# Revit family: CLEVERTRONICS L10 OPTIMUM LIFELIGHT PRO_non_hosted_R16
name_source: partatom
category: Lighting Fixtures
revit_build: Autodesk Revit LT 2016 (Build: 20150220_1215(x64)
units: mm (PartAtom-declared; Revit-internal decimal feet)

## family parameters
Always vertical = Yes
Cut with Voids When Loaded = No
Light Source = Yes
OmniClass Number = 23.80.70.00
OmniClass Title = Lighting
Part Type = Normal
Room Calculation Point = No
Round Connector Dimension = Use Diameter
Shared = No
Work Plane-Based = No

## types (1)
- LLIFE-PRO-SMC
    AS/NZ2293 Classification = C0=D63 C90=D63
    Catalogue Number = LLIFE-PRO-SMC
    Charging Method = Intelligent current limited constant voltage charger
    Color Filter = 16777215
    Description = Lifelight PRO, High Performance, Cylinder Surface Mount Emergency Light with Lithium Battery Technology
    Dimensions L x W x H = 128mm (D), 252mm (L)
    Dimming Lamp Color Temperature Shift = <None>
    IP Rating = IP20
    Lamp = 2 x 3W LED (Lifetime warranty on the lamp head and loom assembly)
2 x 3W LED (Lifetime warranty on the lamp head and loom assembly)
No dome cover required
    Mounting = Surface Mount
    Operating Mode = Non-Maintained
    Operating Temperature = 1 to 40C (Ambient)
    Operating Voltage = 240V 50Hz
    Photometric Web File = ll14604 - ZLIFE-PRO.IES
    Power Consumption = 0.4W (standby) 2.2W (max during 16 hour charge)
    Testing System = Manual Test Switch
    Tilt Angle = 90.00°

## geometry (parser evidence)
native form markers: Sweep x3
no freeform markers — native parametric forms only
